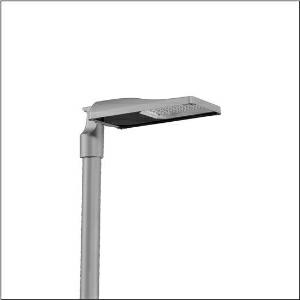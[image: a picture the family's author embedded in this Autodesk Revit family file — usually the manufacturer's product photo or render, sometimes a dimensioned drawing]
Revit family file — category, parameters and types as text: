
# Revit family: streetlight_sl_31_mini___st1_0a_5xh2d3ab08ga_301b
name_source: partatom
category: Lighting Fixtures
units: mm (PartAtom-declared; Revit-internal decimal feet)

## family parameters
Cut with Voids When Loaded = No
Host = Face
Light Source = No
Part Type = Normal
Room Calculation Point = No
Round Connector Dimension = Use Diameter
Shared = No

## types (1)
- --- (1 x LED, 5710 lm, 37.3 W, 3000K)
    Apparent Load = 37 VA
    CIE Flux Codes = 37 72 97 100 100
    Color Rendering = 70
    Color Temperature = 3000K
    Default Elevation = 1800 mm
    Description = Streetlight SL 31 mini Easy LST mast luminaire for post-top, side-entry; light control with lens of PMMA; light distribution: ST1.0a, direct asymmetric distribution, for standard-compliant lighting for roads and squares; LED: luminous flux: 5.710lm, light colour: 730, colour temperature: 3000K; luminous efficacy: 153,1lm/W; control: pre-setting: linear dimming characteristic, flexible luminous flux parameterisation, time-dependent luminous flux control, constant luminous flux control, power reduction, intelligent temperature release in ECG and LED module, overheat protection; luminaire housing, of diecast aluminium, Siteco® metallic grey (DB 702S), corrosivity category C5 high according to DIN EN ISO 12944; cover of toughened safety glass, transparent, mast flange of diecast aluminium, Siteco® metallic grey (DB 702S), spigot size: 76/60mm, mast flange included unmounted; with cable H07RN-F 3x 1.5mm², cable length: 6,5m, connection cable pre-assembled; mains connection: 220..240V, AC, 50/60Hz; power consumption (at start of service life): 37,3W / (at end of service life): 38,7W / (with reduced operation 50%): 17,5W; protection rating (complete): IP66; insulation class (complete): insulation class II (safety insulation); impact resistance: IK10; certification: CE, ENEC, ENEC+, VDE, UKCA; permissible operating ambient temperature for outdoor applications: -40..+50°C; packaging unit: 1 piece

Light Distribution: ST1.0a
    Height = 76 mm
    Lamp = 1 x LED
    Lamp Light Flux = 5710 lm
    Lamp Power = 37.3 W
    Lamp count = 1
    Length = 547 mm
    Luminous efficacy = 153 lm/W
    Manufacturer = Siteco
    ModVariant = No
    Model = 5XH2D3AB08GA
    Number of Poles = 1
    OnlyDefault = Yes
    Power Factor = 1
    Product Name = Streetlight SL 31 mini | ST1.0a
    Product group = mast luminaire | pylon top
    ProductGroupID = 6100
    Protection Class = Protection class II
    Protection Degree = IP 66
    RLX_Detail_Level = 1
    RLX_Emergency_Light_Flux = 0 lm
    RLX_Emergency_Type = 0
    RLX_Emergency_Type_DB = No
    RlxData = <blob elided: 39569 chars, md5=a8cc09c0>
    Socket = socket
    Standby Power = 0 W
    System Light Flux = 5710 lm
    System Power = 37 W
    Type Comments = factory setting: luminous flux: 100 % | dim-lin: 254 | 386 mA
    Type Image = l_1300326.jpg
    URL = http://relux.com
    VarID = @adj_075371
    Voltage = 0 V
    Weight = 0.00 kg
    Width = 265 mm

## geometry (parser evidence)
native form markers: Blend x4, Sweep x10
no freeform markers — native parametric forms only
